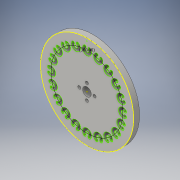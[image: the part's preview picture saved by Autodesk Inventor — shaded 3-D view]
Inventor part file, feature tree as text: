
AUTODESK INVENTOR PART (.ipt)
format: ipt  version: 2016 SP2 (Build 200236200, 236)  size: 280,064 bytes
history: native  units: in
note: dims shown in document units (in); Inventor stores cm internally (conversion verified against a paired STEP export)
features: extrude x3, sketch x2
ambient origin geometry x8: Origin, YZ Plane, XZ Plane, XY Plane, X Axis, Y Axis, Z Axis, Center Point
bodies: Solid1 (feature_tree)
feature tree (5):
  extrude  "Extrusion1"  Depth=0.354in
  sketch  "Sketch2"  dims[d3=0.125in d4=1.5748in d6=360.0deg d8=0.25in d9=0.0in d21=0.25in d22=0.0in d36=7.874in d38=360.0deg d40=0.25in d41=0.0in]
  extrude  "Extrusion2"  Depth=0.25in TaperAngle=360.0deg
  extrude  "Extrusion3"  Depth=0.25in TaperAngle=0.0deg
  sketch  "Sketch1"  dims[d0=3.843in d1=0.354in]
